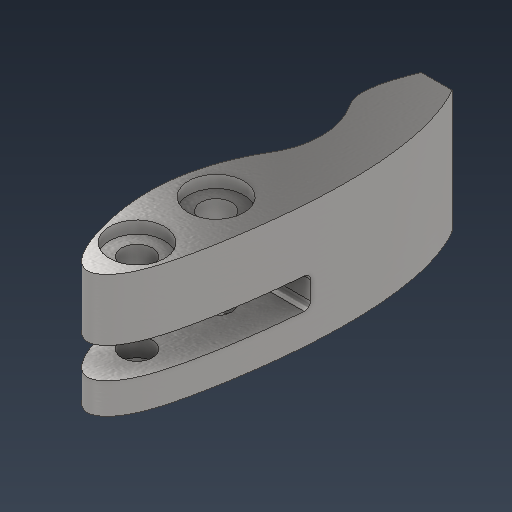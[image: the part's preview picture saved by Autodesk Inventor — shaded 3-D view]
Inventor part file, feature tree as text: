
AUTODESK INVENTOR PART (.ipt)
format: ipt  version: 2021 (Build 250183000, 183)  size: 238,080 bytes
history: native  units: mm
features: sketch x5, extrude x4, hole x1, plane x1, fillet x1, projected_geometry x1
ambient origin geometry x8: Origin, YZ Plane, XZ Plane, XY Plane, X Axis, Y Axis, Z Axis, Center Point
bodies: Solid1 (feature_tree)
feature tree (13):
  extrude  "Extrusion1"  TaperAngle=0.0deg  [1 undecoded]
  hole  "Hole1"  [1 undecoded]
  plane  "Work Plane1"
  extrude  "Extrusion2"  Depth=2.0mm
  fillet  "Fillet1"  Radius=2.0mm
  extrude  "Extrusion3"  Depth=5.0mm
  extrude  "Extrusion4"  Depth=12.133mm
  sketch  "Sketch1"  dims[d0=47.112mm d1=0.0mm]
  sketch  "Sketch2"  dims[d2=12.113mm d3=30.0mm]
  sketch  "Sketch3"  dims[d4=12.887mm d5=12.113mm d6=2.0mm]
  projected_geometry  "Projected Loop1"
  sketch  "Sketch4"  dims[d7=2.0mm d8=5.0mm]
  sketch  "Sketch5"  dims[d9=20.0mm d10=0.0mm d11=12.133mm d12=0.0mm d13=12.877mm d14=5.0mm d15=6.0mm d16=4.0mm d17=2.0mm d18=90.0deg d19=8.0mm d20=20.594885mm d22=5.0mm d23=20.0mm d24=10.0mm d25=50.0mm d26=10.0mm d27=0.0mm d28=1.0mm d29=5.0mm d30=4.5mm d31=2.0mm d32=2.0mm d33=2.0mm d34=0.0mm d35=2.0mm d36=2.0mm d37=2.0mm d38=0.0mm]
note: 2 required parameter values undecoded (feature->parameter linkage not recoverable at this tier; creation-order binding heuristic only, values carry confidence <= 0.55)
